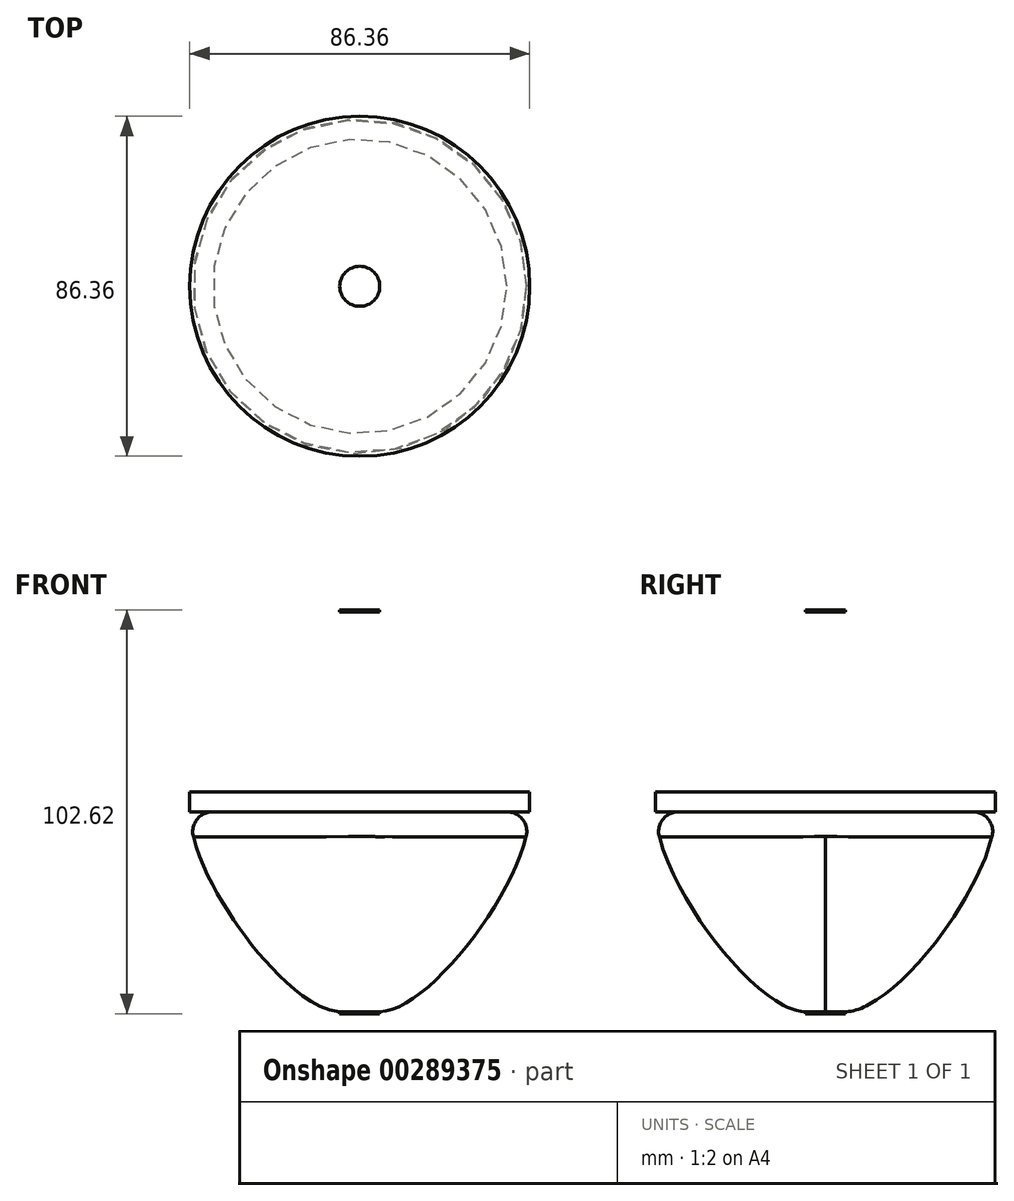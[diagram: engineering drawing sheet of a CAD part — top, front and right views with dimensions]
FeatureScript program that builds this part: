
annotation { "Feature Type Name" : "Feature", "Feature Type Description" : "" }
export const myFeature = defineFeature(function(context is Context, id is Id, definition is map)
    precondition{}
    {
        {
            var Q0;
            Q0=qCreatedBy(makeId("Top.planeOp"),FACE);
            cPlane(context, id + "F0", {"entities" : qUnion([Q0]), "cplaneType" : CPlaneType.OFFSET, "offset" : 50.8 * mm, "width" : 152.4 * mm, "height" : 152.4 * mm});
        }
        {
            var Q0;
            Q0=qCreatedBy(id+"F0.planeOp",FACE);
            var sketch = newSketch(context, id + "F1", { "sketchPlane" : qUnion([Q0])});
            skCircle(sketch, "E0", {"center": v(0, 0) * mm, "radius": 5.08 * mm});
            skLineSegment(sketch, "E1", {"start": v(0, 0) * mm, "end": v(5.08, 0) * mm});
            skSolve(sketch);
        }
        {
            var Q0;
            Q0=qCreatedBy(makeId("Top.planeOp"),FACE);
            cPlane(context, id + "F2", {"entities" : qUnion([Q0]), "cplaneType" : CPlaneType.OFFSET, "offset" : 50.8 * mm, "oppositeDirection" : true, "width" : 152.4 * mm, "height" : 152.4 * mm});
        }
        {
            var Q0;
            Q0=qCreatedBy(id+"F2.planeOp",FACE);
            var sketch = newSketch(context, id + "F3", { "sketchPlane" : qUnion([Q0])});
            skCircle(sketch, "E2", {"center": v(0, 0) * mm, "radius": 5.08 * mm});
            skLineSegment(sketch, "E3", {"start": v(0, 0) * mm, "end": v(5.08, 0) * mm});
            skSolve(sketch);
        }
        {
            var Q0;
            Q0=qCreatedBy(makeId("Top.planeOp"),FACE);
            var sketch = newSketch(context, id + "F4", { "sketchPlane" : qUnion([Q0])});
            skCircle(sketch, "E4", {"center": v(0, 0) * mm, "radius": 43.18 * mm});
            skLineSegment(sketch, "E5", {"start": v(0, 0) * mm, "end": v(0, -43.18) * mm});
            skSolve(sketch);
        }
        {
            var Q0;
            Q0=makeQuery(id+"F3.imprint","IMPRINT",FACE,{"disambiguationData":[TD([[makeQuery(id+"F3.imprint","IMPRINT",EDGE,{"derivedFrom":sQuery(id+"F3.wireOp",EDGE,"E2")}),1.0]])]});
            extrude(context, id + "F5", {"entities" : qUnion([Q0]), "oppositeDirection" : true, "depth" : 0.5 * mm});
        }
        {
            var Q0;
            Q0=makeQuery(id+"F1.imprint","IMPRINT",FACE,{"disambiguationData":[TD([[makeQuery(id+"F1.imprint","IMPRINT",EDGE,{"derivedFrom":sQuery(id+"F1.wireOp",EDGE,"E0")}),1.0]])]});
            extrude(context, id + "F6", {"entities" : qUnion([Q0]), "depth" : 0.5 * mm});
        }
        {
            var Q0;
            Q0=makeQuery(id+"F4.imprint","IMPRINT",FACE,{"disambiguationData":[TD([[makeQuery(id+"F4.imprint","IMPRINT",EDGE,{"derivedFrom":sQuery(id+"F4.wireOp",EDGE,"E4")}),1.0]])]});
            extrude(context, id + "F7", {"entities" : qUnion([Q0]), "depth" : 5.08 * mm});
        }
        {
            var Q0;
            Q0=makeQuery(id+"F4.imprint","IMPRINT",FACE,{"disambiguationData":[TD([[makeQuery(id+"F4.imprint","IMPRINT",EDGE,{"derivedFrom":sQuery(id+"F4.wireOp",EDGE,"E4")}),1.0]])]});
            var Q1;
            Q1=makeQuery(id+"F3.imprint","IMPRINT",FACE,{"disambiguationData":[TD([[makeQuery(id+"F3.imprint","IMPRINT",EDGE,{"derivedFrom":sQuery(id+"F3.wireOp",EDGE,"E2")}),1.0]])]});
            loft(context, id + "F8", {"startCondition" : LoftEndDerivativeType.NORMAL_TO_PROFILE, "startMagnitude" : 1, "endCondition" : LoftEndDerivativeType.TANGENT_TO_PROFILE, "endMagnitude" : 1, "sheetProfilesArray" : [{ "sheetProfileEntities" : qUnion([Q0]) }, { "sheetProfileEntities" : qUnion([Q1]) }]});
        }
        {
            var Q0;
            Q0=makeQuery(id+"F8.opLoft","MID_CAP_EDGE",EDGE,{"disambiguationData":[OSD([sQuery(id+"F4.wireOp",EDGE,"E4")])],"capPos":0.0});
            fillet(context, id + "F9", {"entities" : qUnion([Q0]), "radius" : 5.08 * mm, "tangentPropagation" : true, "allowEdgeOverflow" : false});
        }
    });
